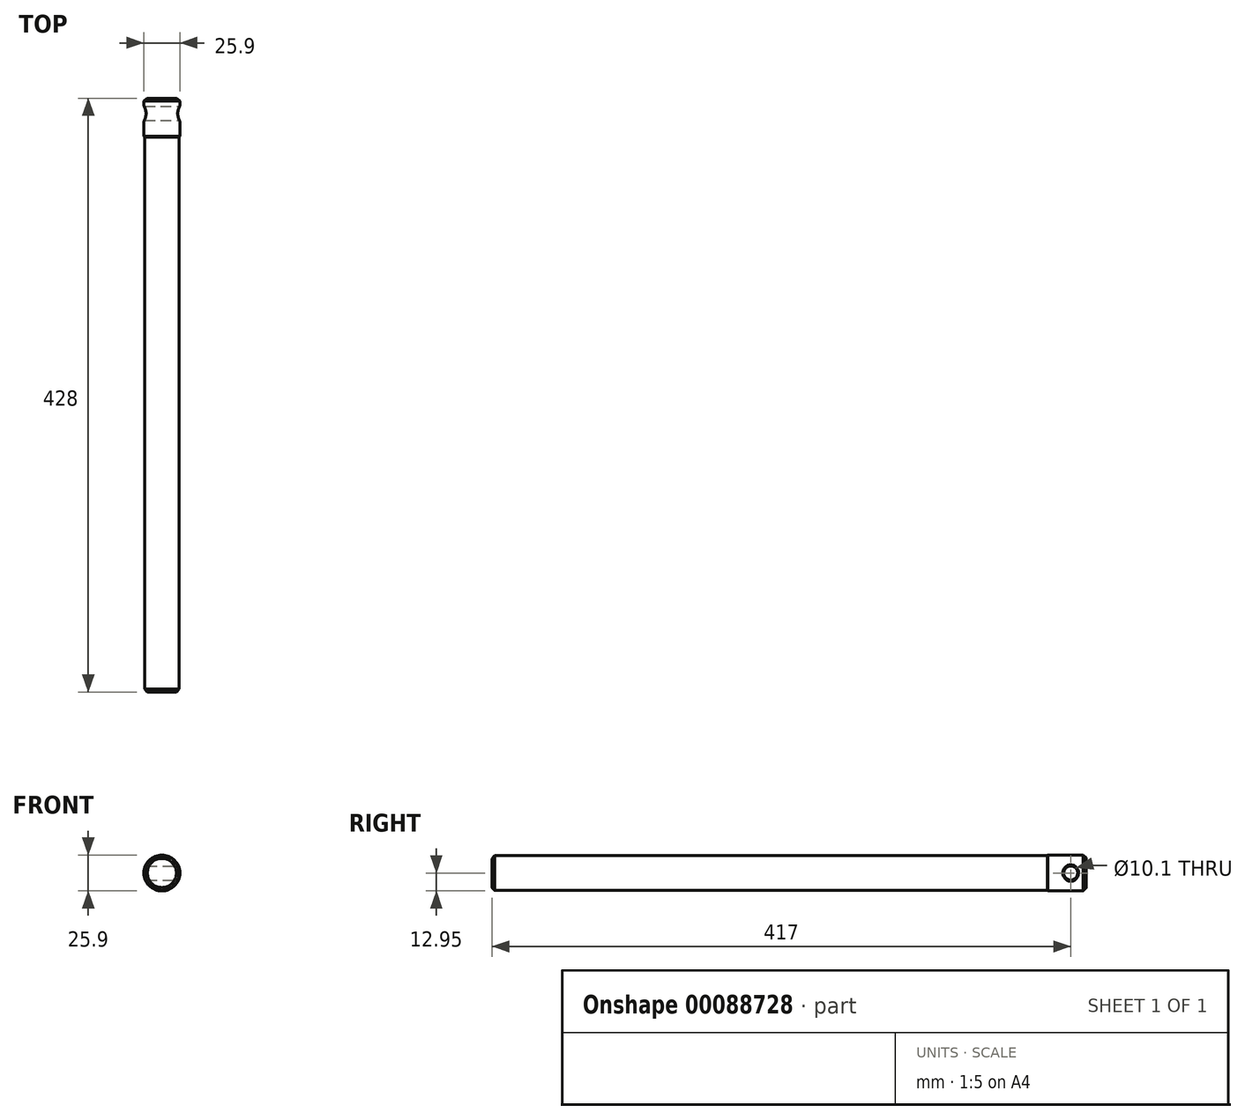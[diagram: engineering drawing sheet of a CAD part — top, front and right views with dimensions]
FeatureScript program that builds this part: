
annotation { "Feature Type Name" : "Feature", "Feature Type Description" : "" }
export const myFeature = defineFeature(function(context is Context, id is Id, definition is map)
    precondition{}
    {
        {
            var Q0;
            Q0=qCreatedBy(makeId("Front.planeOp"),FACE);
            var sketch = newSketch(context, id + "F0", { "sketchPlane" : qUnion([Q0])});
            skCircle(sketch, "E0", {"center": v(0, 0) * mm, "radius": 12.5 * mm});
            skCircle(sketch, "E1", {"center": v(0, 0) * mm, "radius": 12.95 * mm});
            skSolve(sketch);
        }
        {
            var Q0;
            Q0=makeQuery(id+"F0.imprint","IMPRINT",FACE,{"disambiguationData":[TD([[makeQuery(id+"F0.imprint","IMPRINT",EDGE,{"derivedFrom":sQuery(id+"F0.wireOp",EDGE,"E0")}),1.0]])]});
            extrude(context, id + "F1", {"entities" : qUnion([Q0]), "depth" : 400 * mm});
        }
        {
            var Q0;
            Q0 = qSketchRegion(id + "F0", true);
            var Q1;
            Q1=makeQuery(id+"F1.opExtrude","CAP_FACE",FACE,{"disambiguationData":[OSD([sQuery(id+"F0.wireOp",EDGE,"E0")])],"isStart":true});
            extrude(context, id + "F2", {"entities" : qUnion([Q0, Q1]), "operationType" : NewBodyOperationType.ADD, "oppositeDirection" : true, "depth" : 28 * mm});
        }
        {
            var Q0;
            Q0=makeQuery(id+"F1.opExtrude","CAP_EDGE",EDGE,{"disambiguationData":[OSD([sQuery(id+"F0.wireOp",EDGE,"E0")])],"isStart":false});
            chamfer(context, id + "F3", {"entities" : qUnion([Q0]), "width" : 2 * mm, "tangentPropagation" : true});
        }
        {
            var Q0;
            Q0=makeQuery(id+"F2.opExtrude","CAP_EDGE",EDGE,{"disambiguationData":[OSD([sQuery(id+"F0.wireOp",EDGE,"E1")])],"isStart":true});
            chamfer(context, id + "F4", {"entities" : qUnion([Q0]), "width" : 0.5 * mm, "tangentPropagation" : true});
        }
        {
            var Q0;
            Q0=qCreatedBy(makeId("Right.planeOp"),FACE);
            var sketch = newSketch(context, id + "F5", { "sketchPlane" : qUnion([Q0])});
            skCircle(sketch, "E2", {"center": v(17, 0) * mm, "radius": 5.05 * mm});
            skSolve(sketch);
        }
        {
            var Q0;
            Q0 = qSketchRegion(id + "F5", true);
            extrude(context, id + "F6", {"entities" : qUnion([Q0]), "operationType" : NewBodyOperationType.REMOVE, "oppositeDirection" : true, "depth" : 30 * mm, "symmetric" : true});
        }
        {
            var Q0;
            Q0=makeQuery(id+"F2.opExtrude","CAP_EDGE",EDGE,{"disambiguationData":[OSD([sQuery(id+"F0.wireOp",EDGE,"E1")])],"isStart":false});
            chamfer(context, id + "F7", {"entities" : qUnion([Q0]), "width" : 2 * mm, "tangentPropagation" : true});
        }
        {
            var Q0;
            Q0=makeQuery(id+"F6.boolean.opBoolean","INTERSECT",EDGE,{"disambiguationData":[OD(0.0)],"derivedFrom":[makeQuery(id+"F2.opExtrude","SWEPT_FACE",FACE,{"disambiguationData":[OSD([sQuery(id+"F0.wireOp",EDGE,"E1")])]}),makeQuery(id+"F6.opExtrude","SWEPT_FACE",FACE,{"disambiguationData":[OSD([sQuery(id+"F5.wireOp",EDGE,"E2")])]})]});
            var Q1;
            Q1=makeQuery(id+"F6.boolean.opBoolean","INTERSECT",EDGE,{"disambiguationData":[OD(1.0)],"derivedFrom":[makeQuery(id+"F2.opExtrude","SWEPT_FACE",FACE,{"disambiguationData":[OSD([sQuery(id+"F0.wireOp",EDGE,"E1")])]}),makeQuery(id+"F6.opExtrude","SWEPT_FACE",FACE,{"disambiguationData":[OSD([sQuery(id+"F5.wireOp",EDGE,"E2")])]})]});
            chamfer(context, id + "F8", {"entities" : qUnion([Q0, Q1]), "width" : 1 * mm, "tangentPropagation" : true});
        }
    });
